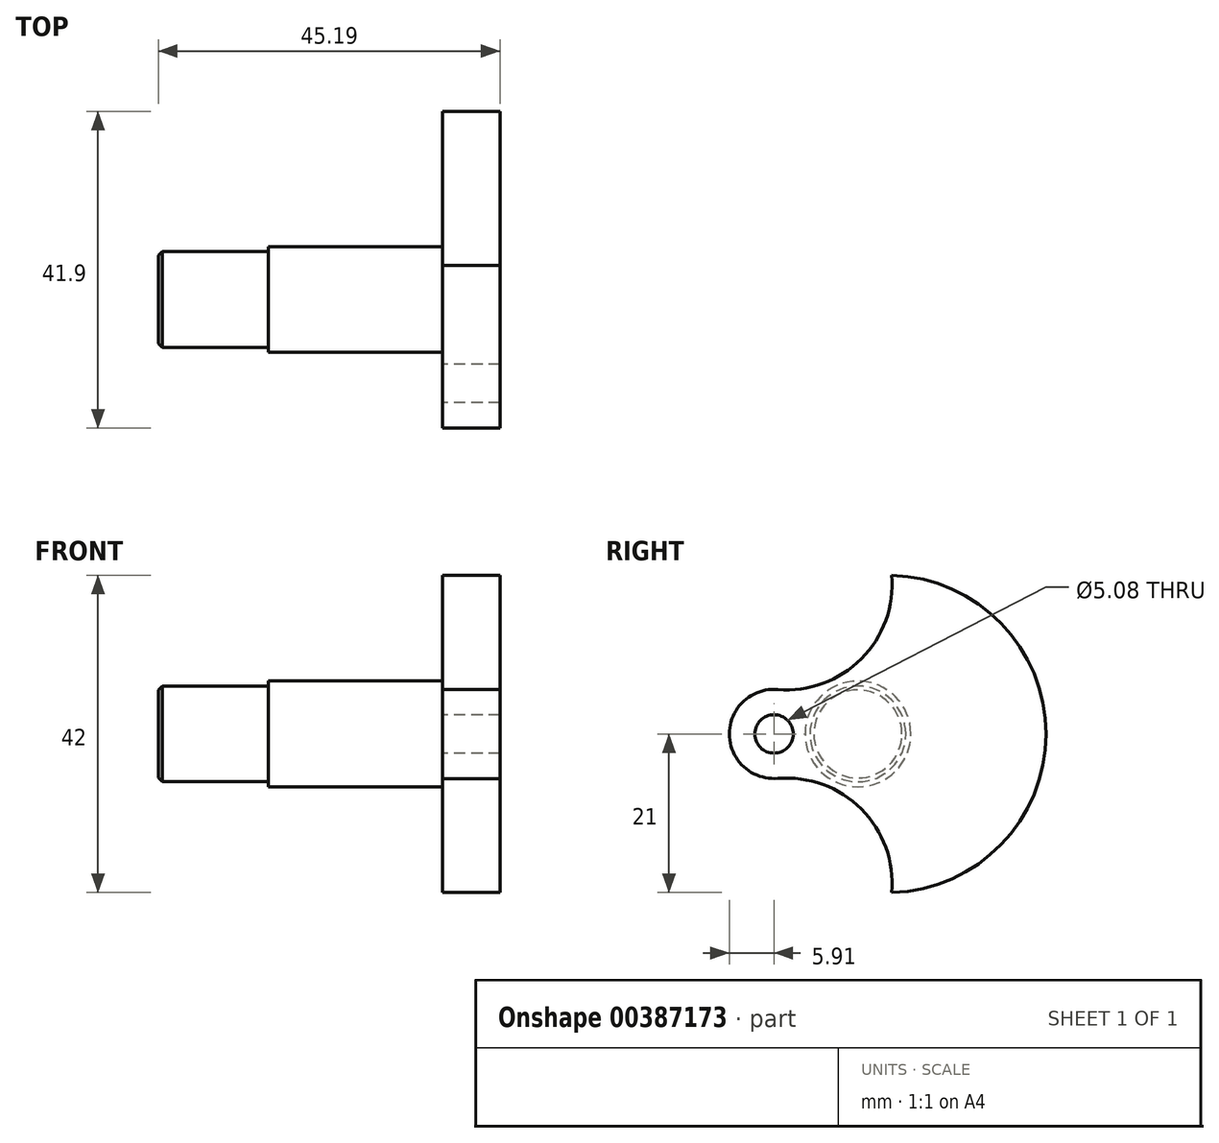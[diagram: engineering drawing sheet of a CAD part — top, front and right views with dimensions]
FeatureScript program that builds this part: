
annotation { "Feature Type Name" : "Feature", "Feature Type Description" : "" }
export const myFeature = defineFeature(function(context is Context, id is Id, definition is map)
    precondition{}
    {
        {
            var Q0;
            Q0=qCreatedBy(makeId("Right.planeOp"),FACE);
            var sketch = newSketch(context, id + "F0", { "sketchPlane" : qUnion([Q0])});
            skLineSegment(sketch, "E0", {"start": v(0, 0) * mm, "end": v(36, 0) * mm});
            skCircle(sketch, "E1", {"center": v(14.99, 0) * mm, "radius": 21 * mm});
            skCircle(sketch, "E2", {"center": v(0, 0) * mm, "radius": 2.54 * mm});
            skLineSegment(sketch, "E3", {"start": v(0, 0) * mm, "end": v(-5.9, 0) * mm});
            skCircle(sketch, "E4", {"center": v(0, 0) * mm, "radius": 5.9 * mm});
            skCircle(sketch, "E5", {"center": v(1.65, 19.83) * mm, "radius": 14 * mm});
            skCircle(sketch, "E6.MirrorC", {"center": v(1.65, -19.83) * mm, "radius": 14 * mm});
            skSolve(sketch);
        }
        {
            var Q0;
            {var subQ0=sQuery(id+"F0.wireOp",EDGE,"E1");var subQ1=sQuery(id+"F0.wireOp",EDGE,"E0");var subQ2=makeQuery(id+"F0.imprint","INTERSECT",VERTEX,{"derivedFrom":[subQ1,subQ0]});Q0=makeQuery(id+"F0.imprint","IMPRINT",FACE,{"disambiguationData":[TD([[makeQuery(id+"F0.imprint","IMPRINT",EDGE,{"disambiguationData":[TD([[subQ2,1.0]])],"derivedFrom":subQ1}),1.0]])]});}
            var Q1;
            {var subQ0=sQuery(id+"F0.wireOp",EDGE,"E1");var subQ1=sQuery(id+"F0.wireOp",EDGE,"E0");var subQ2=makeQuery(id+"F0.imprint","INTERSECT",VERTEX,{"derivedFrom":[subQ1,subQ0]});Q1=makeQuery(id+"F0.imprint","IMPRINT",FACE,{"disambiguationData":[TD([[makeQuery(id+"F0.imprint","IMPRINT",EDGE,{"disambiguationData":[TD([[subQ2,1.0]])],"derivedFrom":subQ1}),-1.0]])]});}
            var Q2;
            {var subQ4=sQuery(id+"F0.wireOp",EDGE,"E2");var subQ5=sQuery(id+"F0.wireOp",EDGE,"E0");var subQ6=makeQuery(id+"F0.imprint","INTERSECT",VERTEX,{"derivedFrom":[subQ5,subQ4]});Q2=makeQuery(id+"F0.imprint","IMPRINT",FACE,{"disambiguationData":[TD([[makeQuery(id+"F0.imprint","IMPRINT",EDGE,{"disambiguationData":[TD([[subQ6,-1.0]])],"derivedFrom":subQ5}),-1.0]])]});}
            var Q3;
            {var subQ1=sQuery(id+"F0.wireOp",EDGE,"E0");var subQ4=sQuery(id+"F0.wireOp",EDGE,"E2");var subQ5=makeQuery(id+"F0.imprint","INTERSECT",VERTEX,{"derivedFrom":[subQ1,subQ4]});Q3=makeQuery(id+"F0.imprint","IMPRINT",FACE,{"disambiguationData":[TD([[makeQuery(id+"F0.imprint","IMPRINT",EDGE,{"disambiguationData":[TD([[subQ5,-1.0]])],"derivedFrom":subQ1}),1.0]])]});}
            extrude(context, id + "F1", {"entities" : qUnion([Q0, Q1, Q2, Q3]), "depth" : 7.62 * mm});
        }
        {
            var Q0;
            Q0=makeQuery(id+"F1.opExtrude","CAP_FACE",FACE,{"disambiguationData":[OSD([sQuery(id+"F0.wireOp",EDGE,"E1"),sQuery(id+"F0.wireOp",EDGE,"E2"),sQuery(id+"F0.wireOp",EDGE,"E4"),sQuery(id+"F0.wireOp",EDGE,"E5"),sQuery(id+"F0.wireOp",EDGE,"E6.MirrorC")])],"isStart":true});
            var sketch = newSketch(context, id + "F2", { "sketchPlane" : qUnion([Q0])});
            skLineSegment(sketch, "E7", {"start": v(5.9, 0) * mm, "end": v(-4.1, 0) * mm});
            skPoint(sketch, "E7.endSnap0", {"position": v(5.9, 0) * mm});
            skCircle(sketch, "E8", {"center": v(-11.1, 0) * mm, "radius": 7 * mm});
            skSolve(sketch);
        }
        {
            var Q0;
            Q0=makeQuery(id+"F2.imprint","IMPRINT",FACE,{"disambiguationData":[TD([[makeQuery(id+"F2.imprint","IMPRINT",EDGE,{"derivedFrom":sQuery(id+"F2.wireOp",EDGE,"E8")}),1.0]])]});
            extrude(context, id + "F3", {"entities" : qUnion([Q0]), "operationType" : NewBodyOperationType.ADD, "depth" : 23.01 * mm});
        }
        {
            var Q0;
            Q0=makeQuery(id+"F3.opExtrude","CAP_FACE",FACE,{"disambiguationData":[OSD([sQuery(id+"F2.wireOp",EDGE,"E8")])],"isStart":false});
            var sketch = newSketch(context, id + "F4", { "sketchPlane" : qUnion([Q0])});
            skCircle(sketch, "E9", {"center": v(-11.1, 0) * mm, "radius": 6.34 * mm});
            skSolve(sketch);
        }
        {
            var Q0;
            Q0=makeQuery(id+"F4.imprint","IMPRINT",FACE,{"disambiguationData":[TD([[makeQuery(id+"F4.imprint","IMPRINT",EDGE,{"derivedFrom":sQuery(id+"F4.wireOp",EDGE,"E9")}),1.0]])]});
            extrude(context, id + "F5", {"entities" : qUnion([Q0]), "operationType" : NewBodyOperationType.ADD, "depth" : 14.55 * mm});
        }
        {
            var Q0;
            Q0=makeQuery(id+"F5.opExtrude","CAP_EDGE",EDGE,{"disambiguationData":[OSD([sQuery(id+"F4.wireOp",EDGE,"E9")])],"isStart":false});
            chamfer(context, id + "F6", {"entities" : qUnion([Q0]), "width" : 0.5 * mm, "tangentPropagation" : true});
        }
    });
